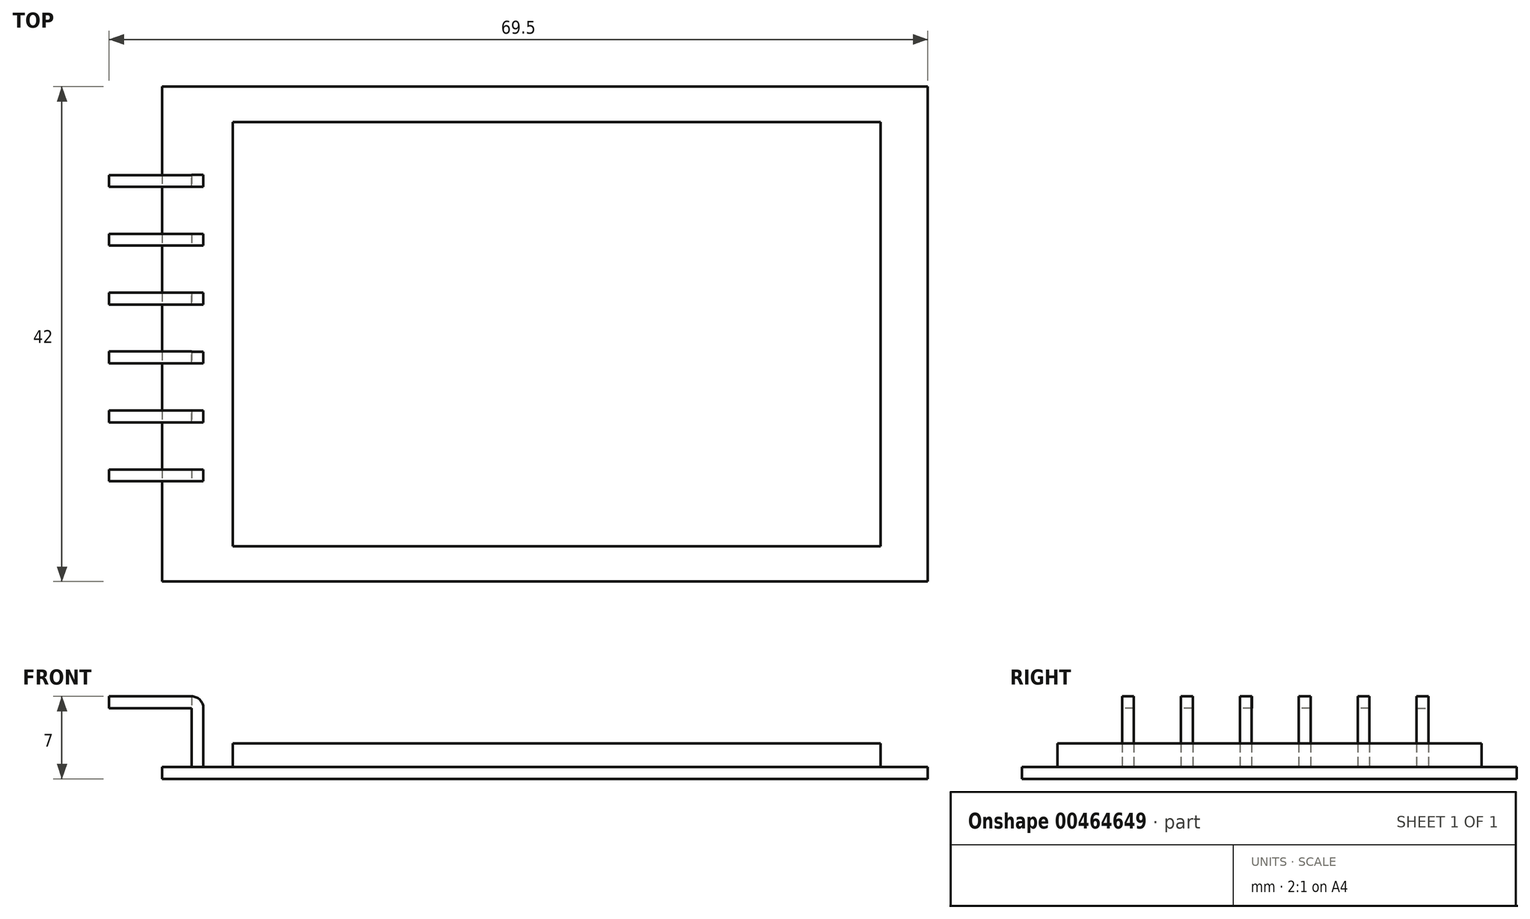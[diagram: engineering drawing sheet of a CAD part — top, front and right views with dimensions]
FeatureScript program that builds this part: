
annotation { "Feature Type Name" : "Feature", "Feature Type Description" : "" }
export const myFeature = defineFeature(function(context is Context, id is Id, definition is map)
    precondition{}
    {
        {
            var Q0;
            Q0=qCreatedBy(makeId("Top.planeOp"),FACE);
            var sketch = newSketch(context, id + "F0", { "sketchPlane" : qUnion([Q0])});
            skLineSegment(sketch, "E0.bottom", {"start": v(27.5, 18) * mm, "end": v(-27.5, 18) * mm});
            skLineSegment(sketch, "E0.top", {"start": v(27.5, -18) * mm, "end": v(-27.5, -18) * mm});
            skLineSegment(sketch, "E0.left", {"start": v(27.5, 18) * mm, "end": v(27.5, -18) * mm});
            skLineSegment(sketch, "E0.right", {"start": v(-27.5, 18) * mm, "end": v(-27.5, -18) * mm});
            skPoint(sketch, "E0.middle", {"position": v(0, 0) * mm});
            skLineSegment(sketch, "E1.bottom", {"start": v(-33.5, 21) * mm, "end": v(31.5, 21) * mm});
            skLineSegment(sketch, "E1.top", {"start": v(-33.5, -21) * mm, "end": v(31.5, -21) * mm});
            skLineSegment(sketch, "E1.left", {"start": v(-33.5, 21) * mm, "end": v(-33.5, -21) * mm});
            skLineSegment(sketch, "E1.right", {"start": v(31.5, 21) * mm, "end": v(31.5, -21) * mm});
            skPoint(sketch, "E2", {"position": v(31.5, 0) * mm});
            skSolve(sketch);
        }
        {
            var Q0;
            Q0=makeQuery(id+"F0.imprint","IMPRINT",FACE,{"disambiguationData":[TD([[makeQuery(id+"F0.imprint","IMPRINT",EDGE,{"derivedFrom":sQuery(id+"F0.wireOp",EDGE,"E0.bottom")}),1.0]])]});
            extrude(context, id + "F1", {"entities" : qUnion([Q0]), "depth" : 2 * mm});
        }
        {
            var Q0;
            Q0=makeQuery(id+"F0.imprint","IMPRINT",FACE,{"disambiguationData":[TD([[makeQuery(id+"F0.imprint","IMPRINT",EDGE,{"derivedFrom":sQuery(id+"F0.wireOp",EDGE,"E0.bottom")}),-1.0]])]});
            var Q1;
            Q1=makeQuery(id+"F0.imprint","IMPRINT",FACE,{"disambiguationData":[TD([[makeQuery(id+"F0.imprint","IMPRINT",EDGE,{"derivedFrom":sQuery(id+"F0.wireOp",EDGE,"E0.bottom")}),1.0]])]});
            extrude(context, id + "F2", {"entities" : qUnion([Q0, Q1]), "oppositeDirection" : true, "depth" : 1 * mm});
        }
        {
            var Q0;
            Q0=makeQuery(id+"F0.imprint","IMPRINT",FACE,{"disambiguationData":[TD([[makeQuery(id+"F0.imprint","IMPRINT",EDGE,{"derivedFrom":sQuery(id+"F0.wireOp",EDGE,"E0.bottom")}),-1.0]])]});
            var sketch = newSketch(context, id + "F3", { "sketchPlane" : qUnion([Q0])});
            skPoint(sketch, "E3", {"position": v(-30.5, 20.27) * mm});
            skLineSegment(sketch, "E4.bottom", {"start": v(-30, 13.5) * mm, "end": v(-31, 13.5) * mm});
            skLineSegment(sketch, "E4.top", {"start": v(-30, 12.5) * mm, "end": v(-31, 12.5) * mm});
            skLineSegment(sketch, "E4.left", {"start": v(-30, 13.5) * mm, "end": v(-30, 12.5) * mm});
            skLineSegment(sketch, "E4.right", {"start": v(-31, 13.5) * mm, "end": v(-31, 12.5) * mm});
            skPoint(sketch, "E4.middle", {"position": v(-30.5, 13) * mm});
            skLineSegment(sketch, "E5.bottom", {"start": v(-30, 7.5) * mm, "end": v(-31, 7.5) * mm});
            skLineSegment(sketch, "E5.top", {"start": v(-30, 8.5) * mm, "end": v(-31, 8.5) * mm});
            skLineSegment(sketch, "E5.left", {"start": v(-30, 7.5) * mm, "end": v(-30, 8.5) * mm});
            skLineSegment(sketch, "E5.right", {"start": v(-31, 7.5) * mm, "end": v(-31, 8.5) * mm});
            skPoint(sketch, "E5.middle", {"position": v(-30.5, 8) * mm});
            skLineSegment(sketch, "E6.bottom", {"start": v(-30, 2.5) * mm, "end": v(-31, 2.5) * mm});
            skLineSegment(sketch, "E6.top", {"start": v(-30, 3.5) * mm, "end": v(-31, 3.5) * mm});
            skLineSegment(sketch, "E6.left", {"start": v(-30, 2.5) * mm, "end": v(-30, 3.5) * mm});
            skLineSegment(sketch, "E6.right", {"start": v(-31, 2.5) * mm, "end": v(-31, 3.5) * mm});
            skPoint(sketch, "E6.middle", {"position": v(-30.5, 3) * mm});
            skLineSegment(sketch, "E7.bottom", {"start": v(-30, -2.5) * mm, "end": v(-31, -2.5) * mm});
            skLineSegment(sketch, "E7.top", {"start": v(-30, -1.5) * mm, "end": v(-31, -1.5) * mm});
            skLineSegment(sketch, "E7.left", {"start": v(-30, -2.5) * mm, "end": v(-30, -1.5) * mm});
            skLineSegment(sketch, "E7.right", {"start": v(-31, -2.5) * mm, "end": v(-31, -1.5) * mm});
            skPoint(sketch, "E7.middle", {"position": v(-30.5, -2) * mm});
            skLineSegment(sketch, "E8.bottom", {"start": v(-30, -7.5) * mm, "end": v(-31, -7.5) * mm});
            skLineSegment(sketch, "E8.top", {"start": v(-30, -6.5) * mm, "end": v(-31, -6.5) * mm});
            skLineSegment(sketch, "E8.left", {"start": v(-30, -7.5) * mm, "end": v(-30, -6.5) * mm});
            skLineSegment(sketch, "E8.right", {"start": v(-31, -7.5) * mm, "end": v(-31, -6.5) * mm});
            skPoint(sketch, "E8.middle", {"position": v(-30.5, -7) * mm});
            skLineSegment(sketch, "E9.bottom", {"start": v(-30, -12.5) * mm, "end": v(-31, -12.5) * mm});
            skLineSegment(sketch, "E9.top", {"start": v(-30, -11.5) * mm, "end": v(-31, -11.5) * mm});
            skLineSegment(sketch, "E9.left", {"start": v(-30, -12.5) * mm, "end": v(-30, -11.5) * mm});
            skLineSegment(sketch, "E9.right", {"start": v(-31, -12.5) * mm, "end": v(-31, -11.5) * mm});
            skPoint(sketch, "E9.middle", {"position": v(-30.5, -12) * mm});
            skPoint(sketch, "E10", {"position": v(-30.5, 0) * mm});
            skPoint(sketch, "E10.positionSnap0", {"position": v(-30.5, 2.5) * mm});
            skSolve(sketch);
        }
        {
            var Q0;
            Q0 = qSketchRegion(id + "F3", true);
            extrude(context, id + "F4", {"entities" : qUnion([Q0]), "depth" : 6 * mm});
        }
        {
            var Q0;
            Q0=makeQuery(id+"F4.opExtrude","SWEPT_FACE",FACE,{"disambiguationData":[OSD([sQuery(id+"F3.wireOp",EDGE,"E5.right")])]});
            var sketch = newSketch(context, id + "F5", { "sketchPlane" : qUnion([Q0])});
            skLineSegment(sketch, "E11.bottom", {"start": v(-12.5, 6) * mm, "end": v(-13.5, 6) * mm});
            skLineSegment(sketch, "E11.top", {"start": v(-12.5, 5) * mm, "end": v(-13.5, 5) * mm});
            skLineSegment(sketch, "E11.left", {"start": v(-12.5, 6) * mm, "end": v(-12.5, 5) * mm});
            skLineSegment(sketch, "E11.right", {"start": v(-13.5, 6) * mm, "end": v(-13.5, 5) * mm});
            skLineSegment(sketch, "E12.bottom", {"start": v(-8.5, 6) * mm, "end": v(-7.5, 6) * mm});
            skLineSegment(sketch, "E12.top", {"start": v(-8.5, 5) * mm, "end": v(-7.5, 5) * mm});
            skLineSegment(sketch, "E12.left", {"start": v(-8.5, 6) * mm, "end": v(-8.5, 5) * mm});
            skLineSegment(sketch, "E12.right", {"start": v(-7.5, 6) * mm, "end": v(-7.5, 5) * mm});
            skLineSegment(sketch, "E13.bottom", {"start": v(-3.5, 6) * mm, "end": v(-2.5, 6) * mm});
            skLineSegment(sketch, "E13.top", {"start": v(-3.5, 5) * mm, "end": v(-2.5, 5) * mm});
            skLineSegment(sketch, "E13.left", {"start": v(-3.5, 6) * mm, "end": v(-3.5, 5) * mm});
            skLineSegment(sketch, "E13.right", {"start": v(-2.5, 6) * mm, "end": v(-2.5, 5) * mm});
            skLineSegment(sketch, "E14.bottom", {"start": v(1.48, 6) * mm, "end": v(2.48, 6) * mm});
            skLineSegment(sketch, "E14.top", {"start": v(1.48, 5) * mm, "end": v(2.48, 5) * mm});
            skLineSegment(sketch, "E14.left", {"start": v(1.48, 6) * mm, "end": v(1.48, 5) * mm});
            skLineSegment(sketch, "E14.right", {"start": v(2.48, 6) * mm, "end": v(2.48, 5) * mm});
            skLineSegment(sketch, "E15.bottom", {"start": v(6.5, 6) * mm, "end": v(7.5, 6) * mm});
            skLineSegment(sketch, "E15.top", {"start": v(6.5, 5) * mm, "end": v(7.5, 5) * mm});
            skLineSegment(sketch, "E15.left", {"start": v(6.5, 6) * mm, "end": v(6.5, 5) * mm});
            skLineSegment(sketch, "E15.right", {"start": v(7.5, 6) * mm, "end": v(7.5, 5) * mm});
            skLineSegment(sketch, "E16.bottom", {"start": v(11.5, 6) * mm, "end": v(12.5, 6) * mm});
            skLineSegment(sketch, "E16.top", {"start": v(11.5, 5) * mm, "end": v(12.5, 5) * mm});
            skLineSegment(sketch, "E16.left", {"start": v(11.5, 6) * mm, "end": v(11.5, 5) * mm});
            skLineSegment(sketch, "E16.right", {"start": v(12.5, 6) * mm, "end": v(12.5, 5) * mm});
            skSolve(sketch);
        }
        {
            var Q0;
            Q0=makeQuery(id+"F5.imprint","IMPRINT",FACE,{"disambiguationData":[TD([[makeQuery(id+"F5.imprint","IMPRINT",EDGE,{"derivedFrom":sQuery(id+"F5.wireOp",EDGE,"E11.bottom")}),1.0]])]});
            var Q1;
            Q1=makeQuery(id+"F5.imprint","IMPRINT",FACE,{"disambiguationData":[TD([[makeQuery(id+"F5.imprint","IMPRINT",EDGE,{"derivedFrom":sQuery(id+"F5.wireOp",EDGE,"E12.bottom")}),1.0]])]});
            var Q2;
            Q2=makeQuery(id+"F5.imprint","IMPRINT",FACE,{"disambiguationData":[TD([[makeQuery(id+"F5.imprint","IMPRINT",EDGE,{"derivedFrom":sQuery(id+"F5.wireOp",EDGE,"E13.bottom")}),-1.0]])]});
            var Q3;
            Q3=makeQuery(id+"F5.imprint","IMPRINT",FACE,{"disambiguationData":[TD([[makeQuery(id+"F5.imprint","IMPRINT",EDGE,{"derivedFrom":sQuery(id+"F5.wireOp",EDGE,"E14.bottom")}),-1.0]])]});
            var Q4;
            Q4=makeQuery(id+"F5.imprint","IMPRINT",FACE,{"disambiguationData":[TD([[makeQuery(id+"F5.imprint","IMPRINT",EDGE,{"derivedFrom":sQuery(id+"F5.wireOp",EDGE,"E15.bottom")}),-1.0]])]});
            var Q5;
            Q5=makeQuery(id+"F5.imprint","IMPRINT",FACE,{"disambiguationData":[TD([[makeQuery(id+"F5.imprint","IMPRINT",EDGE,{"derivedFrom":sQuery(id+"F5.wireOp",EDGE,"E16.bottom")}),-1.0]])]});
            extrude(context, id + "F6", {"entities" : qUnion([Q0, Q1, Q2, Q3, Q4, Q5]), "operationType" : NewBodyOperationType.ADD, "depth" : 7 * mm});
        }
        {
            var Q0;
            Q0=makeQuery(id+"F4.opExtrude","CAP_EDGE",EDGE,{"disambiguationData":[OSD([sQuery(id+"F3.wireOp",EDGE,"E4.left")])],"isStart":false});
            var Q1;
            Q1=makeQuery(id+"F4.opExtrude","CAP_EDGE",EDGE,{"disambiguationData":[OSD([sQuery(id+"F3.wireOp",EDGE,"E5.left")])],"isStart":false});
            var Q2;
            Q2=makeQuery(id+"F4.opExtrude","CAP_EDGE",EDGE,{"disambiguationData":[OSD([sQuery(id+"F3.wireOp",EDGE,"E6.left")])],"isStart":false});
            var Q3;
            Q3=makeQuery(id+"F4.opExtrude","CAP_EDGE",EDGE,{"disambiguationData":[OSD([sQuery(id+"F3.wireOp",EDGE,"E7.left")])],"isStart":false});
            var Q4;
            Q4=makeQuery(id+"F4.opExtrude","CAP_EDGE",EDGE,{"disambiguationData":[OSD([sQuery(id+"F3.wireOp",EDGE,"E8.left")])],"isStart":false});
            var Q5;
            Q5=makeQuery(id+"F4.opExtrude","CAP_EDGE",EDGE,{"disambiguationData":[OSD([sQuery(id+"F3.wireOp",EDGE,"E9.left")])],"isStart":false});
            fillet(context, id + "F7", {"entities" : qUnion([Q0, Q1, Q2, Q3, Q4, Q5]), "radius" : 1 * mm, "tangentPropagation" : true, "allowEdgeOverflow" : false});
        }
    });
